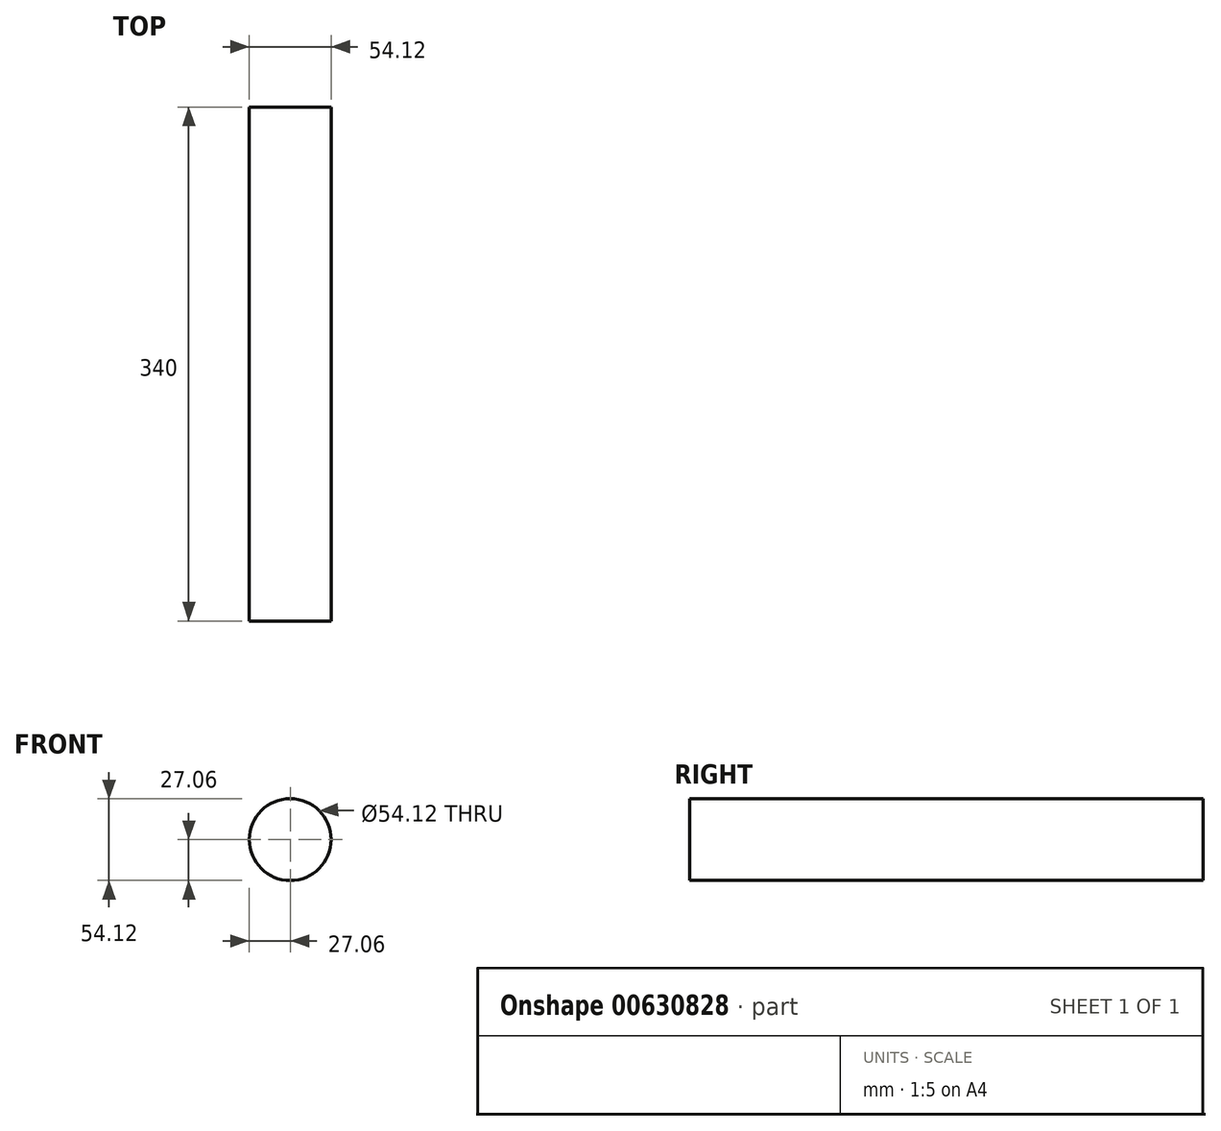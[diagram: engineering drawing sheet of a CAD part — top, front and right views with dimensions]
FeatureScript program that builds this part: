
annotation { "Feature Type Name" : "Feature", "Feature Type Description" : "" }
export const myFeature = defineFeature(function(context is Context, id is Id, definition is map)
    precondition{}
    {
        {
            var Q0;
            Q0=qCreatedBy(makeId("Front.planeOp"),FACE);
            var sketch = newSketch(context, id + "F0", { "sketchPlane" : qUnion([Q0])});
            skCircle(sketch, "E0", {"center": v(0, 0) * mm, "radius": 27.06 * mm});
            skSolve(sketch);
        }
        {
            var Q0;
            Q0=sQuery(id+"F0.wireOp",EDGE,"E0");
            extrude(context, id + "F1", {"bodyType" : ToolBodyType.SURFACE, "surfaceEntities" : qUnion([Q0]), "oppositeDirection" : true, "depth" : 340 * mm, "offsetDistance" : 25 * mm});
        }
    });
